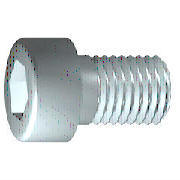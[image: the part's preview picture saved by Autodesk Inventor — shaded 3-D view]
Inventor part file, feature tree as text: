
AUTODESK INVENTOR PART (.ipt)
format: ipt  version: 2024.3 (Build 283343000, 343)  size: 192,512 bytes
history: native  units: mm (DEFAULTED — no unit token found)
features: extrude x1, plane x1, fillet x1
ambient origin geometry x7: Origin, YZ Plane, XY Plane, X Axis, Y Axis, Z Axis, Center Point
bodies: Solid1 (feature_tree), Body (feature_tree)
feature tree (3):
  extrude  "Slot"  Depth=17.5mm
  plane  "Work Plane1"
  fillet  "Fillet2"  Radius=0.61355mm
